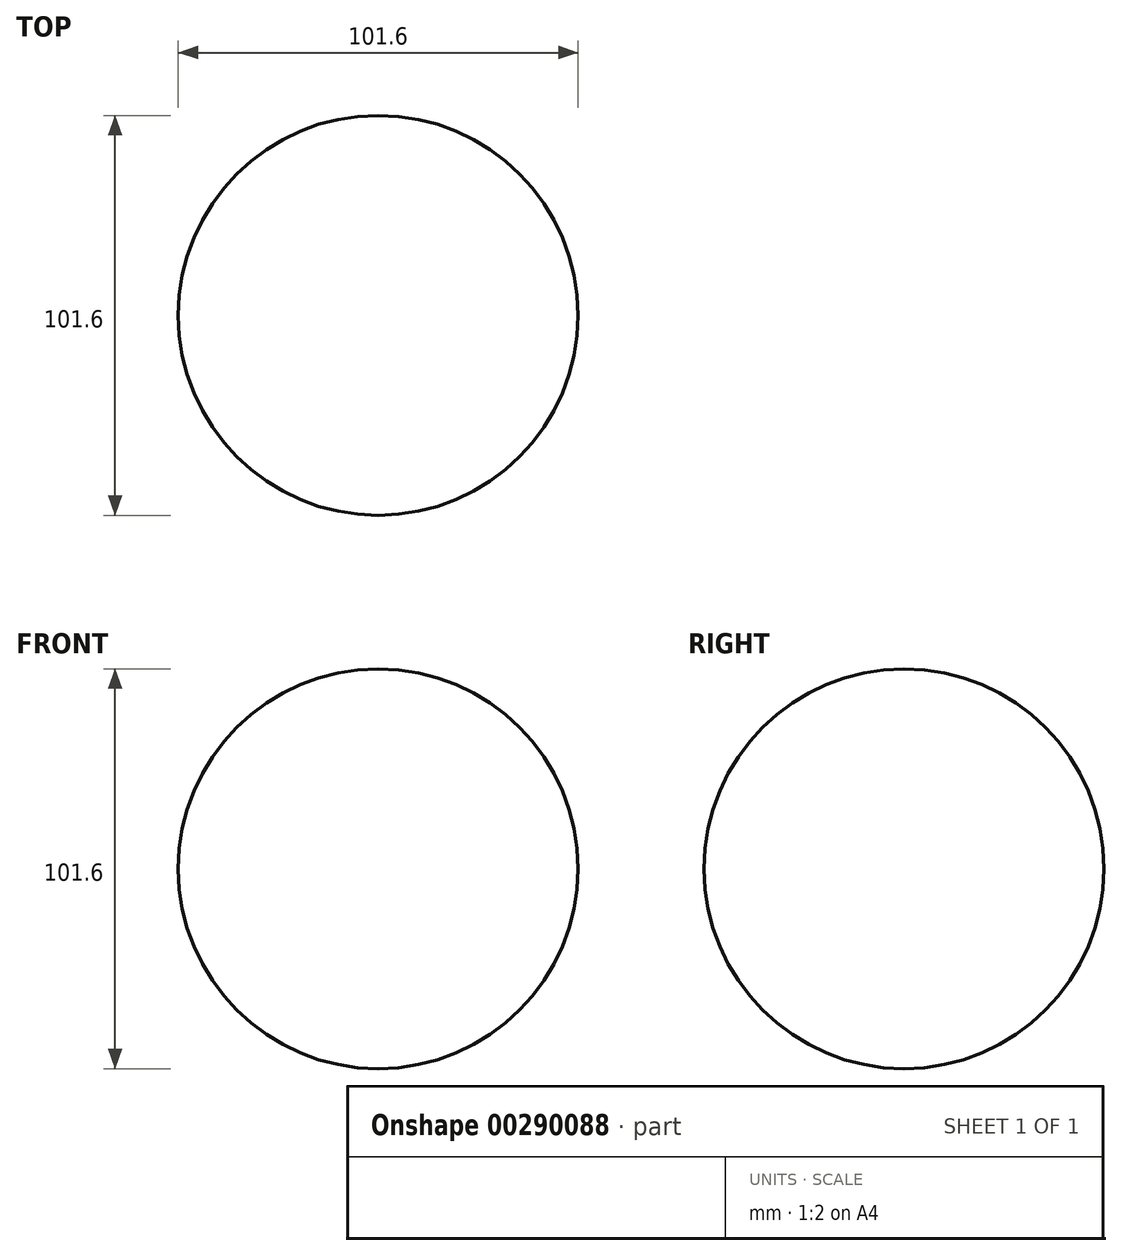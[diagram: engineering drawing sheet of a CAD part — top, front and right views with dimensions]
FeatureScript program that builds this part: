
annotation { "Feature Type Name" : "Feature", "Feature Type Description" : "" }
export const myFeature = defineFeature(function(context is Context, id is Id, definition is map)
    precondition{}
    {
        {
            var Q0;
            Q0=qCreatedBy(makeId("Top.planeOp"),FACE);
            var sketch = newSketch(context, id + "F0", { "sketchPlane" : qUnion([Q0])});
            skArc(sketch, "E0", {"start": v(0, 50.8) * mm, "mid": v(-50.8, 0) * mm, "end": v(0, -50.8) * mm});
            skLineSegment(sketch, "E1", {"start": v(0, 50.8) * mm, "end": v(0, -50.8) * mm});
            skSolve(sketch);
        }
        {
            var Q0;
            Q0=makeQuery(id+"F0.imprint","IMPRINT",FACE,{"disambiguationData":[TD([[makeQuery(id+"F0.imprint","IMPRINT",EDGE,{"derivedFrom":sQuery(id+"F0.wireOp",EDGE,"E0")}),1.0]])]});
            var Q1;
            Q1=sQuery(id+"F0.wireOp",EDGE,"E1");
            revolve(context, id + "F1", {"entities" : qUnion([Q0]), "axis" : qUnion([Q1]), "revolveType" : RevolveType.FULL});
        }
    });
